# Revit family: MDM
name_source: partatom
category: Lighting Fixtures
revit_build: Autodesk Revit 2014 (Build: 20130308_1515(x64)
units: mm (PartAtom-declared; Revit-internal decimal feet)

## types (2) — shared parameters
Apparent Load = 0 VA
Application = Healthcare
Certification = UL1598,cCSAus,CSA,Wet Loation Listed, IP65 w/Door
Color Filter = 16777215
Color Rendering Index = 80 CRI , 90CRI
Default Elevation = 48 "
Description = The MediMode provides the primary lighting needs for the patient environment. The ambient and reading compartment provide a low-glare even illumination while the dedicated compartment for exam lighting delivers 100+ fc for critical examination functions. A full lensed door is available with stainless steel hinge or secured by screws.
Dimming Lamp Color Temperature Shift = <None>
Emit Shape Visible in Rendering = No
Emit from Rectangle Width = 24 "
Features = Provides ambient, reading and examination illumination for the patient bed environment
PowerHUBB™ PoE Lighting and Control options available
Grid and flange applications available
All compartments are lensed for visual comfort and ease of cleaning
An IP65 rated, full lensed door option further seals the luminairefor enhanced protection
The optical frame provides tool-less access to the electrical components for easy servicing
Standard antimicrobial finish
Fixture Life = 60,000 HRS
Glass = Hubbell - Glass
LED = Hubbell - Glass
Lamp = LED
Manufacturer = Healthcare Solutions
Model = MediMode™ PowerHUBB™
Photometric Web File = generic
Product Documentation Link = https://hubbellcdn.com
Product Material = Paint - Hubbell - Matte White
Product Page URL = https://www.hubbell.com
Tilt Angle = 60.00°
URL = https://www.hubbell.com
Voltage = 120-277V
Warranty = Five year warranty (Terms and Conditions Apply)
Width = 24 "

## per-type parameters (varying)
| type | Emit from Rectangle Length | End | Inner End | Inner Start | Length | Start | Watt |
| MDM22 | 24 " | 12 " | 11.5 " | -11.5 " | 24 " | -12 " | 25 W |
| MDM24 | 48 " | 24 " | 23.5 " | -23.5 " | 48 " | -24 " | 41 W |

## geometry (parser evidence)
native form markers: Sweep x5
no freeform markers — native parametric forms only
